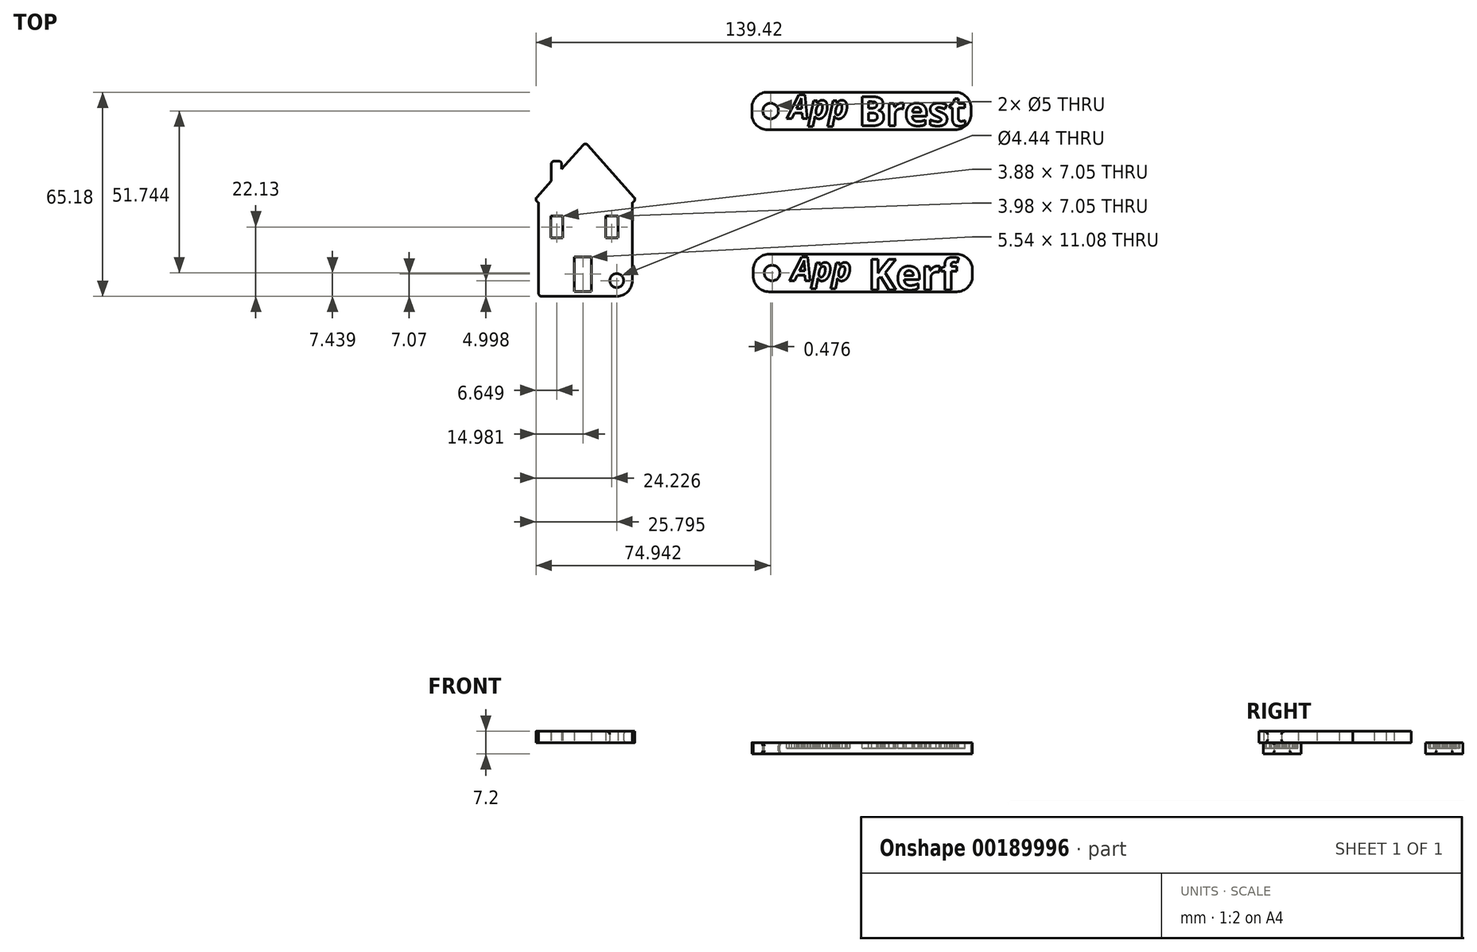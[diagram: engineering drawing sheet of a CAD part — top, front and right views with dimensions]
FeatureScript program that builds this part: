
annotation { "Feature Type Name" : "Feature", "Feature Type Description" : "" }
export const myFeature = defineFeature(function(context is Context, id is Id, definition is map)
    precondition{}
    {
        {
            var Q0;
            Q0=qCreatedBy(makeId("Top.planeOp"),FACE);
            var sketch = newSketch(context, id + "F0", { "sketchPlane" : qUnion([Q0])});
            skText(sketch, "E0", { "text": "Brest", "fontName": "OpenSans-Bold.ttf"});
            skText(sketch, "E1", { "text": "Kerf", "fontName": "OpenSans-Bold.ttf"});
            skText(sketch, "E2", { "text": "App", "fontName": "OpenSans-BoldItalic.ttf"});
            skText(sketch, "E3", { "text": "App", "fontName": "OpenSans-BoldItalic.ttf"});
            skLineSegment(sketch, "E4.bottom", {"start": v(852.3, 12.63) * mm, "end": v(922.3, 12.63) * mm});
            skLineSegment(sketch, "E4.top", {"start": v(852.3, 0.63) * mm, "end": v(922.3, 0.63) * mm});
            skLineSegment(sketch, "E4.left", {"start": v(852.3, 12.63) * mm, "end": v(852.3, 0.63) * mm});
            skLineSegment(sketch, "E4.right", {"start": v(922.3, 12.63) * mm, "end": v(922.3, 0.63) * mm});
            skLineSegment(sketch, "E5.bottom", {"start": v(852.77, -39.11) * mm, "end": v(922.77, -39.11) * mm});
            skLineSegment(sketch, "E5.top", {"start": v(852.77, -51.11) * mm, "end": v(922.77, -51.11) * mm});
            skLineSegment(sketch, "E5.left", {"start": v(852.77, -39.11) * mm, "end": v(852.77, -51.11) * mm});
            skLineSegment(sketch, "E5.right", {"start": v(922.77, -39.11) * mm, "end": v(922.77, -51.11) * mm});
            skLineSegment(sketch, "E6", {"start": v(852.77, -45.11) * mm, "end": v(858.77, -45.11) * mm});
            skCircle(sketch, "E7", {"center": v(858.77, -45.11) * mm, "radius": 2.5 * mm});
            skLineSegment(sketch, "E8", {"start": v(852.3, 6.63) * mm, "end": v(858.3, 6.63) * mm});
            skCircle(sketch, "E9", {"center": v(858.3, 6.63) * mm, "radius": 2.5 * mm});
            const initialGuessF0  = {"E0": [0.8864, 0.00195, 1, 0, 0.00935], "E1": [0.8893, -0.05048, 1, 0, 0.0098], "E2": [0.864, 0.00423, 1, 0, 0.00758], "E3": [0.86494, -0.04758, 1, 0, 0.00758]};
            skSetInitialGuess(sketch, initialGuessF0);
            skSolve(sketch);
        }
        {
            var Q0;
            Q0=makeQuery(id+"F0.imprint","IMPRINT",FACE,{"disambiguationData":[TD([[makeQuery(id+"F0.imprint","IMPRINT",EDGE,{"derivedFrom":sQuery(id+"F0.wireOp",EDGE,"E0.sketch_text.stroke-58")}),-1.0]])]});
            var Q1;
            Q1=makeQuery(id+"F0.imprint","IMPRINT",FACE,{"disambiguationData":[TD([[makeQuery(id+"F0.imprint","IMPRINT",EDGE,{"derivedFrom":sQuery(id+"F0.wireOp",EDGE,"E0.sketch_text.stroke-84")}),-1.0]])]});
            var Q2;
            Q2=makeQuery(id+"F0.imprint","IMPRINT",FACE,{"disambiguationData":[TD([[makeQuery(id+"F0.imprint","IMPRINT",EDGE,{"derivedFrom":sQuery(id+"F0.wireOp",EDGE,"E2.sketch_text.stroke-0")}),-1.0]])]});
            var Q3;
            Q3=makeQuery(id+"F0.imprint","IMPRINT",FACE,{"disambiguationData":[TD([[makeQuery(id+"F0.imprint","IMPRINT",EDGE,{"derivedFrom":sQuery(id+"F0.wireOp",EDGE,"E0.sketch_text.stroke-38")}),-1.0]])]});
            var Q4;
            Q4=makeQuery(id+"F0.imprint","IMPRINT",FACE,{"disambiguationData":[TD([[makeQuery(id+"F0.imprint","IMPRINT",EDGE,{"derivedFrom":sQuery(id+"F0.wireOp",EDGE,"E2.sketch_text.stroke-14")}),-1.0]])]});
            var Q5;
            Q5=makeQuery(id+"F0.imprint","IMPRINT",FACE,{"disambiguationData":[TD([[makeQuery(id+"F0.imprint","IMPRINT",EDGE,{"derivedFrom":sQuery(id+"F0.wireOp",EDGE,"E2.sketch_text.stroke-39")}),-1.0]])]});
            var Q6;
            Q6=makeQuery(id+"F0.imprint","IMPRINT",FACE,{"disambiguationData":[TD([[makeQuery(id+"F0.imprint","IMPRINT",EDGE,{"derivedFrom":sQuery(id+"F0.wireOp",EDGE,"E0.sketch_text.stroke-12")}),1.0]])]});
            var Q7;
            Q7=makeQuery(id+"F0.imprint","IMPRINT",FACE,{"disambiguationData":[TD([[makeQuery(id+"F0.imprint","IMPRINT",EDGE,{"derivedFrom":sQuery(id+"F0.wireOp",EDGE,"E0.sketch_text.stroke-19")}),1.0]])]});
            var Q8;
            Q8=makeQuery(id+"F0.imprint","IMPRINT",FACE,{"disambiguationData":[TD([[makeQuery(id+"F0.imprint","IMPRINT",EDGE,{"derivedFrom":sQuery(id+"F0.wireOp",EDGE,"E0.sketch_text.stroke-25")}),-1.0]])]});
            var Q9;
            Q9=makeQuery(id+"F0.imprint","IMPRINT",FACE,{"disambiguationData":[TD([[makeQuery(id+"F0.imprint","IMPRINT",EDGE,{"derivedFrom":sQuery(id+"F0.wireOp",EDGE,"E2.sketch_text.stroke-55")}),1.0]])]});
            var Q10;
            Q10=makeQuery(id+"F0.imprint","IMPRINT",FACE,{"disambiguationData":[TD([[makeQuery(id+"F0.imprint","IMPRINT",EDGE,{"derivedFrom":sQuery(id+"F0.wireOp",EDGE,"E0.sketch_text.stroke-0")}),1.0]])]});
            var Q11;
            Q11=makeQuery(id+"F0.imprint","IMPRINT",FACE,{"disambiguationData":[TD([[makeQuery(id+"F0.imprint","IMPRINT",EDGE,{"derivedFrom":sQuery(id+"F0.wireOp",EDGE,"E0.sketch_text.stroke-0")}),-1.0]])]});
            var Q12;
            Q12=makeQuery(id+"F0.imprint","IMPRINT",FACE,{"disambiguationData":[TD([[makeQuery(id+"F0.imprint","IMPRINT",EDGE,{"derivedFrom":sQuery(id+"F0.wireOp",EDGE,"E0.sketch_text.stroke-38")}),1.0]])]});
            var Q13;
            Q13=makeQuery(id+"F0.imprint","IMPRINT",FACE,{"disambiguationData":[TD([[makeQuery(id+"F0.imprint","IMPRINT",EDGE,{"derivedFrom":sQuery(id+"F0.wireOp",EDGE,"E2.sketch_text.stroke-8")}),1.0]])]});
            var Q14;
            Q14=makeQuery(id+"F0.imprint","IMPRINT",FACE,{"disambiguationData":[TD([[makeQuery(id+"F0.imprint","IMPRINT",EDGE,{"derivedFrom":sQuery(id+"F0.wireOp",EDGE,"E2.sketch_text.stroke-30")}),1.0]])]});
            var Q15;
            Q15=makeQuery(id+"F0.imprint","IMPRINT",FACE,{"disambiguationData":[TD([[makeQuery(id+"F0.imprint","IMPRINT",EDGE,{"derivedFrom":sQuery(id+"F0.wireOp",EDGE,"E1.sketch_text.stroke-0")}),1.0]])]});
            var Q16;
            Q16 = qSketchRegion(id + "F0", true);
            var Q17;
            Q17=makeQuery(id+"F0.imprint","IMPRINT",FACE,{"disambiguationData":[TD([[makeQuery(id+"F0.imprint","IMPRINT",EDGE,{"derivedFrom":sQuery(id+"F0.wireOp",EDGE,"E1.sketch_text.stroke-0")}),-1.0]])]});
            var Q18;
            Q18=makeQuery(id+"F0.imprint","IMPRINT",FACE,{"disambiguationData":[TD([[makeQuery(id+"F0.imprint","IMPRINT",EDGE,{"derivedFrom":sQuery(id+"F0.wireOp",EDGE,"E1.sketch_text.stroke-13")}),-1.0]])]});
            var Q19;
            Q19=makeQuery(id+"F0.imprint","IMPRINT",FACE,{"disambiguationData":[TD([[makeQuery(id+"F0.imprint","IMPRINT",EDGE,{"derivedFrom":sQuery(id+"F0.wireOp",EDGE,"E3.sketch_text.stroke-30")}),1.0]])]});
            var Q20;
            Q20=makeQuery(id+"F0.imprint","IMPRINT",FACE,{"disambiguationData":[TD([[makeQuery(id+"F0.imprint","IMPRINT",EDGE,{"derivedFrom":sQuery(id+"F0.wireOp",EDGE,"E1.sketch_text.stroke-33")}),-1.0]])]});
            var Q21;
            Q21=makeQuery(id+"F0.imprint","IMPRINT",FACE,{"disambiguationData":[TD([[makeQuery(id+"F0.imprint","IMPRINT",EDGE,{"derivedFrom":sQuery(id+"F0.wireOp",EDGE,"E1.sketch_text.stroke-46")}),-1.0]])]});
            var Q22;
            Q22=makeQuery(id+"F0.imprint","IMPRINT",FACE,{"disambiguationData":[TD([[makeQuery(id+"F0.imprint","IMPRINT",EDGE,{"derivedFrom":sQuery(id+"F0.wireOp",EDGE,"E3.sketch_text.stroke-0")}),-1.0]])]});
            var Q23;
            Q23=makeQuery(id+"F0.imprint","IMPRINT",FACE,{"disambiguationData":[TD([[makeQuery(id+"F0.imprint","IMPRINT",EDGE,{"derivedFrom":sQuery(id+"F0.wireOp",EDGE,"E3.sketch_text.stroke-14")}),-1.0]])]});
            var Q24;
            Q24=makeQuery(id+"F0.imprint","IMPRINT",FACE,{"disambiguationData":[TD([[makeQuery(id+"F0.imprint","IMPRINT",EDGE,{"derivedFrom":sQuery(id+"F0.wireOp",EDGE,"E3.sketch_text.stroke-39")}),-1.0]])]});
            var Q25;
            Q25=makeQuery(id+"F0.imprint","IMPRINT",FACE,{"disambiguationData":[TD([[makeQuery(id+"F0.imprint","IMPRINT",EDGE,{"derivedFrom":sQuery(id+"F0.wireOp",EDGE,"E3.sketch_text.stroke-55")}),1.0]])]});
            var Q26;
            Q26=makeQuery(id+"F0.imprint","IMPRINT",FACE,{"disambiguationData":[TD([[makeQuery(id+"F0.imprint","IMPRINT",EDGE,{"derivedFrom":sQuery(id+"F0.wireOp",EDGE,"E3.sketch_text.stroke-8")}),1.0]])]});
            var Q27;
            Q27=makeQuery(id+"F0.imprint","IMPRINT",FACE,{"disambiguationData":[TD([[makeQuery(id+"F0.imprint","IMPRINT",EDGE,{"derivedFrom":sQuery(id+"F0.wireOp",EDGE,"E1.sketch_text.stroke-13")}),1.0]])]});
            extrude(context, id + "F1", {"entities" : qUnion([Q0, Q1, Q2, Q3, Q4, Q5, Q6, Q7, Q8, Q9, Q10, Q11, Q12, Q13, Q14, Q15, Q16, Q17, Q18, Q19, Q20, Q21, Q22, Q23, Q24, Q25, Q26, Q27]), "oppositeDirection" : true, "depth" : 3.6 * mm});
        }
        {
            var Q0;
            Q0=makeQuery(id+"F0.imprint","IMPRINT",FACE,{"disambiguationData":[TD([[makeQuery(id+"F0.imprint","IMPRINT",EDGE,{"derivedFrom":sQuery(id+"F0.wireOp",EDGE,"E2.sketch_text.stroke-0")}),-1.0]])]});
            var Q1;
            Q1=makeQuery(id+"F0.imprint","IMPRINT",FACE,{"disambiguationData":[TD([[makeQuery(id+"F0.imprint","IMPRINT",EDGE,{"derivedFrom":sQuery(id+"F0.wireOp",EDGE,"E2.sketch_text.stroke-14")}),-1.0]])]});
            var Q2;
            Q2=makeQuery(id+"F0.imprint","IMPRINT",FACE,{"disambiguationData":[TD([[makeQuery(id+"F0.imprint","IMPRINT",EDGE,{"derivedFrom":sQuery(id+"F0.wireOp",EDGE,"E2.sketch_text.stroke-39")}),-1.0]])]});
            var Q3;
            Q3=makeQuery(id+"F0.imprint","IMPRINT",FACE,{"disambiguationData":[TD([[makeQuery(id+"F0.imprint","IMPRINT",EDGE,{"derivedFrom":sQuery(id+"F0.wireOp",EDGE,"E0.sketch_text.stroke-0")}),-1.0]])]});
            var Q4;
            Q4=makeQuery(id+"F0.imprint","IMPRINT",FACE,{"disambiguationData":[TD([[makeQuery(id+"F0.imprint","IMPRINT",EDGE,{"derivedFrom":sQuery(id+"F0.wireOp",EDGE,"E0.sketch_text.stroke-25")}),-1.0]])]});
            var Q5;
            Q5=makeQuery(id+"F0.imprint","IMPRINT",FACE,{"disambiguationData":[TD([[makeQuery(id+"F0.imprint","IMPRINT",EDGE,{"derivedFrom":sQuery(id+"F0.wireOp",EDGE,"E0.sketch_text.stroke-38")}),-1.0]])]});
            var Q6;
            Q6=makeQuery(id+"F0.imprint","IMPRINT",FACE,{"disambiguationData":[TD([[makeQuery(id+"F0.imprint","IMPRINT",EDGE,{"derivedFrom":sQuery(id+"F0.wireOp",EDGE,"E0.sketch_text.stroke-58")}),-1.0]])]});
            var Q7;
            Q7=makeQuery(id+"F0.imprint","IMPRINT",FACE,{"disambiguationData":[TD([[makeQuery(id+"F0.imprint","IMPRINT",EDGE,{"derivedFrom":sQuery(id+"F0.wireOp",EDGE,"E0.sketch_text.stroke-84")}),-1.0]])]});
            var Q8;
            Q8=makeQuery(id+"F0.imprint","IMPRINT",FACE,{"disambiguationData":[TD([[makeQuery(id+"F0.imprint","IMPRINT",EDGE,{"derivedFrom":sQuery(id+"F0.wireOp",EDGE,"E1.sketch_text.stroke-46")}),-1.0]])]});
            var Q9;
            Q9=makeQuery(id+"F0.imprint","IMPRINT",FACE,{"disambiguationData":[TD([[makeQuery(id+"F0.imprint","IMPRINT",EDGE,{"derivedFrom":sQuery(id+"F0.wireOp",EDGE,"E1.sketch_text.stroke-33")}),-1.0]])]});
            var Q10;
            Q10=makeQuery(id+"F0.imprint","IMPRINT",FACE,{"disambiguationData":[TD([[makeQuery(id+"F0.imprint","IMPRINT",EDGE,{"derivedFrom":sQuery(id+"F0.wireOp",EDGE,"E1.sketch_text.stroke-0")}),-1.0]])]});
            var Q11;
            Q11=makeQuery(id+"F0.imprint","IMPRINT",FACE,{"disambiguationData":[TD([[makeQuery(id+"F0.imprint","IMPRINT",EDGE,{"derivedFrom":sQuery(id+"F0.wireOp",EDGE,"E1.sketch_text.stroke-13")}),-1.0]])]});
            var Q12;
            Q12=makeQuery(id+"F0.imprint","IMPRINT",FACE,{"disambiguationData":[TD([[makeQuery(id+"F0.imprint","IMPRINT",EDGE,{"derivedFrom":sQuery(id+"F0.wireOp",EDGE,"E3.sketch_text.stroke-39")}),-1.0]])]});
            var Q13;
            Q13=makeQuery(id+"F0.imprint","IMPRINT",FACE,{"disambiguationData":[TD([[makeQuery(id+"F0.imprint","IMPRINT",EDGE,{"derivedFrom":sQuery(id+"F0.wireOp",EDGE,"E3.sketch_text.stroke-14")}),-1.0]])]});
            var Q14;
            Q14=makeQuery(id+"F0.imprint","IMPRINT",FACE,{"disambiguationData":[TD([[makeQuery(id+"F0.imprint","IMPRINT",EDGE,{"derivedFrom":sQuery(id+"F0.wireOp",EDGE,"E3.sketch_text.stroke-0")}),-1.0]])]});
            extrude(context, id + "F2", {"entities" : qUnion([Q0, Q1, Q2, Q3, Q4, Q5, Q6, Q7, Q8, Q9, Q10, Q11, Q12, Q13, Q14]), "operationType" : NewBodyOperationType.REMOVE, "oppositeDirection" : true, "depth" : 1.8 * mm});
        }
        {
            var Q0;
            Q0=makeQuery(id+"F1.opExtrude","SWEPT_EDGE",EDGE,{"disambiguationData":[OSD([sQuery(id+"F0.wireOp",EDGE,"E5.top"),sQuery(id+"F0.wireOp",EDGE,"E5.right")])]});
            var Q1;
            Q1=makeQuery(id+"F1.opExtrude","SWEPT_EDGE",EDGE,{"disambiguationData":[OSD([sQuery(id+"F0.wireOp",EDGE,"E5.bottom"),sQuery(id+"F0.wireOp",EDGE,"E5.right")])]});
            var Q2;
            Q2=makeQuery(id+"F1.opExtrude","SWEPT_EDGE",EDGE,{"disambiguationData":[OSD([sQuery(id+"F0.wireOp",EDGE,"E4.top"),sQuery(id+"F0.wireOp",EDGE,"E4.right")])]});
            var Q3;
            Q3=makeQuery(id+"F1.opExtrude","SWEPT_EDGE",EDGE,{"disambiguationData":[OSD([sQuery(id+"F0.wireOp",EDGE,"E4.bottom"),sQuery(id+"F0.wireOp",EDGE,"E4.right")])]});
            var Q4;
            Q4=makeQuery(id+"F1.opExtrude","SWEPT_EDGE",EDGE,{"disambiguationData":[OSD([sQuery(id+"F0.wireOp",EDGE,"E5.top"),sQuery(id+"F0.wireOp",EDGE,"E5.left")])]});
            var Q5;
            Q5=makeQuery(id+"F1.opExtrude","SWEPT_EDGE",EDGE,{"disambiguationData":[OSD([sQuery(id+"F0.wireOp",EDGE,"E5.bottom"),sQuery(id+"F0.wireOp",EDGE,"E5.left")])]});
            var Q6;
            Q6=makeQuery(id+"F1.opExtrude","SWEPT_EDGE",EDGE,{"disambiguationData":[OSD([sQuery(id+"F0.wireOp",EDGE,"E4.top"),sQuery(id+"F0.wireOp",EDGE,"E4.left")])]});
            var Q7;
            Q7=makeQuery(id+"F1.opExtrude","SWEPT_EDGE",EDGE,{"disambiguationData":[OSD([sQuery(id+"F0.wireOp",EDGE,"E4.bottom"),sQuery(id+"F0.wireOp",EDGE,"E4.left")])]});
            fillet(context, id + "F3", {"entities" : qUnion([Q0, Q1, Q2, Q3, Q4, Q5, Q6, Q7]), "radius" : 5 * mm, "tangentPropagation" : true, "allowEdgeOverflow" : false});
        }
        {
            var Q0;
            Q0=makeQuery(id+"F1.opExtrude","CAP_EDGE",EDGE,{"disambiguationData":[OSD([sQuery(id+"F0.wireOp",EDGE,"E9")])],"isStart":true});
            var Q1;
            Q1=makeQuery(id+"F1.opExtrude","CAP_EDGE",EDGE,{"disambiguationData":[OSD([sQuery(id+"F0.wireOp",EDGE,"E9")])],"isStart":false});
            var Q2;
            Q2=makeQuery(id+"F1.opExtrude","CAP_EDGE",EDGE,{"disambiguationData":[OSD([sQuery(id+"F0.wireOp",EDGE,"E7")])],"isStart":false});
            var Q3;
            Q3=makeQuery(id+"F1.opExtrude","CAP_EDGE",EDGE,{"disambiguationData":[OSD([sQuery(id+"F0.wireOp",EDGE,"E7")])],"isStart":true});
            fillet(context, id + "F4", {"entities" : qUnion([Q0, Q1, Q2, Q3]), "radius" : 1 * mm, "tangentPropagation" : true, "allowEdgeOverflow" : false});
        }
        {
            var Q0;
            Q0=qCreatedBy(makeId("Top.planeOp"),FACE);
            var sketch = newSketch(context, id + "F5", { "sketchPlane" : qUnion([Q0])});
            skLineSegment(sketch, "E10.bottom", {"start": v(784.14, -22.55) * mm, "end": v(814.14, -22.55) * mm});
            skLineSegment(sketch, "E10.top", {"start": v(784.14, -52.55) * mm, "end": v(814.14, -52.55) * mm});
            skLineSegment(sketch, "E10.left", {"start": v(784.14, -22.55) * mm, "end": v(784.14, -52.55) * mm});
            skLineSegment(sketch, "E10.right", {"start": v(814.14, -22.55) * mm, "end": v(814.14, -52.55) * mm});
            skLineSegment(sketch, "E11", {"start": v(784.14, -22.55) * mm, "end": v(782.14, -22.55) * mm});
            skLineSegment(sketch, "E12", {"start": v(782.14, -22.55) * mm, "end": v(799.14, -3.4) * mm});
            skPoint(sketch, "E12.endSnap0", {"position": v(799.14, -22.55) * mm});
            skLineSegment(sketch, "E13", {"start": v(799.14, -3.4) * mm, "end": v(816.14, -22.55) * mm});
            skLineSegment(sketch, "E14", {"start": v(816.14, -22.55) * mm, "end": v(814.14, -22.55) * mm});
            skCircle(sketch, "E15", {"center": v(809.14, -47.55) * mm, "radius": 2.22 * mm});
            skLineSegment(sketch, "E16.bottom", {"start": v(788.06, -26.9) * mm, "end": v(791.94, -26.9) * mm});
            skLineSegment(sketch, "E16.top", {"start": v(788.06, -33.95) * mm, "end": v(791.94, -33.95) * mm});
            skLineSegment(sketch, "E16.left", {"start": v(788.06, -26.9) * mm, "end": v(788.06, -33.95) * mm});
            skLineSegment(sketch, "E16.right", {"start": v(791.94, -26.9) * mm, "end": v(791.94, -33.95) * mm});
            skLineSegment(sketch, "E17.bottom", {"start": v(805.59, -26.9) * mm, "end": v(809.56, -26.9) * mm});
            skLineSegment(sketch, "E17.top", {"start": v(805.59, -33.95) * mm, "end": v(809.56, -33.95) * mm});
            skLineSegment(sketch, "E17.left", {"start": v(805.59, -26.9) * mm, "end": v(805.59, -33.95) * mm});
            skLineSegment(sketch, "E17.right", {"start": v(809.56, -26.9) * mm, "end": v(809.56, -33.95) * mm});
            skLineSegment(sketch, "E18.bottom", {"start": v(795.56, -51.02) * mm, "end": v(801.1, -51.02) * mm});
            skLineSegment(sketch, "E18.top", {"start": v(795.56, -39.94) * mm, "end": v(801.1, -39.94) * mm});
            skLineSegment(sketch, "E18.left", {"start": v(795.56, -51.02) * mm, "end": v(795.56, -39.94) * mm});
            skLineSegment(sketch, "E18.right", {"start": v(801.1, -51.02) * mm, "end": v(801.1, -39.94) * mm});
            skLineSegment(sketch, "E19", {"start": v(788.2, -15.73) * mm, "end": v(788.2, -9.4) * mm});
            skLineSegment(sketch, "E20", {"start": v(788.2, -9.4) * mm, "end": v(791.57, -9.4) * mm});
            skLineSegment(sketch, "E21", {"start": v(791.57, -9.4) * mm, "end": v(791.57, -11.93) * mm});
            skLineSegment(sketch, "E22", {"start": v(809.14, -47.55) * mm, "end": v(814.14, -47.55) * mm});
            skLineSegment(sketch, "E23", {"start": v(809.14, -47.55) * mm, "end": v(809.14, -52.55) * mm});
            skSolve(sketch);
        }
        {
            var Q0;
            Q0=makeQuery(id+"F5.imprint","IMPRINT",FACE,{"disambiguationData":[TD([[makeQuery(id+"F5.imprint","IMPRINT",EDGE,{"derivedFrom":sQuery(id+"F5.wireOp",EDGE,"E10.bottom")}),-1.0]])]});
            var Q1;
            Q1=makeQuery(id+"F5.imprint","IMPRINT",FACE,{"disambiguationData":[TD([[makeQuery(id+"F5.imprint","IMPRINT",EDGE,{"derivedFrom":sQuery(id+"F5.wireOp",EDGE,"E10.bottom")}),1.0]])]});
            var Q2;
            {var subQ0=sQuery(id+"F5.wireOp",EDGE,"E19");Q2=makeQuery(id+"F5.imprint","IMPRINT",FACE,{"disambiguationData":[TD([[makeQuery(id+"F5.imprint","IMPRINT",EDGE,{"derivedFrom":subQ0}),-1.0]])]});}
            var Q3;
            {var subQ1=sQuery(id+"F5.wireOp",EDGE,"E10.right");var subQ6=sQuery(id+"F5.wireOp",EDGE,"E10.top");var subQ9=makeQuery(id+"F5.imprint","INTERSECT",VERTEX,{"derivedFrom":[subQ6,subQ1]});Q3=makeQuery(id+"F5.imprint","IMPRINT",FACE,{"disambiguationData":[TD([[makeQuery(id+"F5.imprint","IMPRINT",EDGE,{"disambiguationData":[TD([[subQ9,1.0]])],"derivedFrom":subQ6}),1.0]])]});}
            extrude(context, id + "F6", {"entities" : qUnion([Q0, Q1, Q2, Q3]), "depth" : 3.6 * mm});
        }
        {
            var Q0;
            Q0=makeQuery(id+"F6.opExtrude","CAP_EDGE",EDGE,{"disambiguationData":[OSD([sQuery(id+"F5.wireOp",EDGE,"E15")])],"isStart":false});
            var Q1;
            Q1=makeQuery(id+"F6.opExtrude","CAP_EDGE",EDGE,{"disambiguationData":[OSD([sQuery(id+"F5.wireOp",EDGE,"E15")])],"isStart":true});
            fillet(context, id + "F7", {"entities" : qUnion([Q0, Q1]), "radius" : 1 * mm, "tangentPropagation" : true, "allowEdgeOverflow" : false});
        }
        {
            var Q0;
            Q0=makeQuery(id+"F6.opExtrude","SWEPT_EDGE",EDGE,{"disambiguationData":[OSD([sQuery(id+"F5.wireOp",EDGE,"E10.top"),sQuery(id+"F5.wireOp",EDGE,"E10.right")])]});
            fillet(context, id + "F8", {"entities" : qUnion([Q0]), "radius" : 5 * mm, "tangentPropagation" : true, "allowEdgeOverflow" : false});
        }
        {
            var Q0;
            Q0=makeQuery(id+"F6.opExtrude","SWEPT_EDGE",EDGE,{"disambiguationData":[OSD([sQuery(id+"F5.wireOp",EDGE,"E10.top"),sQuery(id+"F5.wireOp",EDGE,"E10.left")])]});
            var Q1;
            Q1=makeQuery(id+"F6.opExtrude","SWEPT_EDGE",EDGE,{"disambiguationData":[OSD([sQuery(id+"F5.wireOp",EDGE,"E11"),sQuery(id+"F5.wireOp",EDGE,"E12")])]});
            var Q2;
            Q2=makeQuery(id+"F6.opExtrude","SWEPT_EDGE",EDGE,{"disambiguationData":[OSD([sQuery(id+"F5.wireOp",EDGE,"E19"),sQuery(id+"F5.wireOp",EDGE,"E20")])]});
            var Q3;
            Q3=makeQuery(id+"F6.opExtrude","SWEPT_EDGE",EDGE,{"disambiguationData":[OSD([sQuery(id+"F5.wireOp",EDGE,"E20"),sQuery(id+"F5.wireOp",EDGE,"E21")])]});
            var Q4;
            Q4=makeQuery(id+"F6.opExtrude","SWEPT_EDGE",EDGE,{"disambiguationData":[OSD([sQuery(id+"F5.wireOp",EDGE,"E12"),sQuery(id+"F5.wireOp",EDGE,"E13")])]});
            var Q5;
            Q5=makeQuery(id+"F6.opExtrude","SWEPT_EDGE",EDGE,{"disambiguationData":[OSD([sQuery(id+"F5.wireOp",EDGE,"E13"),sQuery(id+"F5.wireOp",EDGE,"E14")])]});
            fillet(context, id + "F9", {"entities" : qUnion([Q0, Q1, Q2, Q3, Q4, Q5]), "radius" : 1 * mm, "tangentPropagation" : true, "allowEdgeOverflow" : false});
        }
    });
